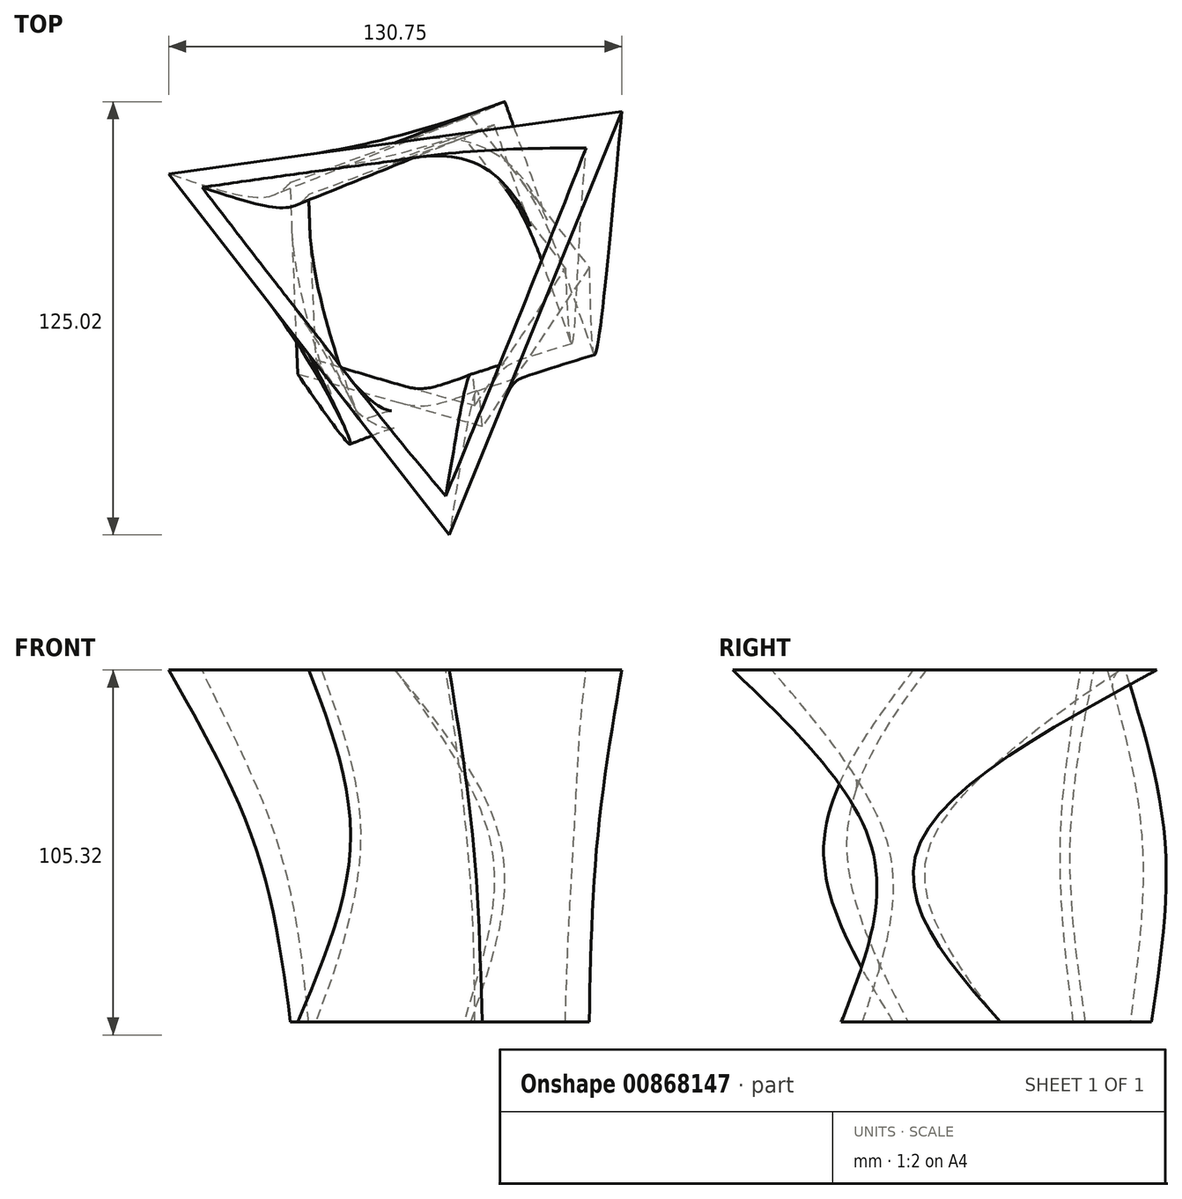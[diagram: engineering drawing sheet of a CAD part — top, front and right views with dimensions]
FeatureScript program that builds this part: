
annotation { "Feature Type Name" : "Feature", "Feature Type Description" : "" }
export const myFeature = defineFeature(function(context is Context, id is Id, definition is map)
    precondition{}
    {
        {
            var Q0;
            Q0=qCreatedBy(makeId("Top.planeOp"),FACE);
            var sketch = newSketch(context, id + "F0", { "sketchPlane" : qUnion([Q0])});
            skCircle(sketch, "E0.cCircle", {"center": v(0, 0) * mm, "radius": 38.1 * mm, "construction": true});
            skLineSegment(sketch, "E0.0", {"start": v(-39.1, 26.24) * mm, "end": v(12.87, 45.3) * mm});
            skLineSegment(sketch, "E0.1", {"start": v(12.87, 45.3) * mm, "end": v(47.06, 1.76) * mm});
            skLineSegment(sketch, "E0.2", {"start": v(47.06, 1.76) * mm, "end": v(16.21, -44.22) * mm});
            skLineSegment(sketch, "E0.3", {"start": v(16.21, -44.22) * mm, "end": v(-37.04, -29.08) * mm});
            skLineSegment(sketch, "E0.4", {"start": v(-37.04, -29.08) * mm, "end": v(-39.1, 26.24) * mm});
            skPoint(sketch, "E0.0.midPoint", {"position": v(-13.12, 35.77) * mm});
            skSolve(sketch);
        }
        {
            var Q0;
            Q0=qCreatedBy(makeId("Top.planeOp"),FACE);
            cPlane(context, id + "F1", {"entities" : qUnion([Q0]), "cplaneType" : CPlaneType.OFFSET, "offset" : 50.8 * mm, "width" : 152.4 * mm, "height" : 152.4 * mm});
        }
        {
            var Q0;
            Q0=qCreatedBy(id+"F1.planeOp",FACE);
            var sketch = newSketch(context, id + "F2", { "sketchPlane" : qUnion([Q0])});
            skCircle(sketch, "E1.cCircle", {"center": v(0, 0) * mm, "radius": 38.1 * mm, "construction": true});
            skLineSegment(sketch, "E1.0", {"start": v(-49.26, 21.84) * mm, "end": v(21.84, 49.26) * mm});
            skLineSegment(sketch, "E1.1", {"start": v(21.84, 49.26) * mm, "end": v(49.26, -21.84) * mm});
            skLineSegment(sketch, "E1.2", {"start": v(49.26, -21.84) * mm, "end": v(-21.84, -49.26) * mm});
            skLineSegment(sketch, "E1.3", {"start": v(-21.84, -49.26) * mm, "end": v(-49.26, 21.84) * mm});
            skPoint(sketch, "E1.0.midPoint", {"position": v(-13.71, 35.55) * mm});
            skLineSegment(sketch, "E2", {"start": v(-21.84, -49.26) * mm, "end": v(21.84, 49.26) * mm, "construction": true});
            skSolve(sketch);
        }
        {
            var Q0;
            Q0=qCreatedBy(id+"F1.planeOp",FACE);
            cPlane(context, id + "F3", {"entities" : qUnion([Q0]), "cplaneType" : CPlaneType.OFFSET, "offset" : 50.8 * mm, "width" : 152.4 * mm, "height" : 152.4 * mm});
        }
        {
            var Q0;
            Q0=qCreatedBy(id+"F3.planeOp",FACE);
            var sketch = newSketch(context, id + "F4", { "sketchPlane" : qUnion([Q0])});
            skCircle(sketch, "E3.cCircle", {"center": v(-3.69, 0) * mm, "radius": 38.1 * mm, "construction": true});
            skLineSegment(sketch, "E3.0", {"start": v(-74.27, 28.73) * mm, "end": v(56.48, 46.76) * mm});
            skLineSegment(sketch, "E3.1", {"start": v(56.48, 46.76) * mm, "end": v(6.72, -75.49) * mm});
            skLineSegment(sketch, "E3.2", {"start": v(6.72, -75.49) * mm, "end": v(-74.27, 28.73) * mm});
            skPoint(sketch, "E3.0.midPoint", {"position": v(-8.9, 37.74) * mm});
            skSolve(sketch);
        }
        {
            var Q0;
            Q0=makeQuery(id+"F0.imprint","IMPRINT",FACE,{"disambiguationData":[TD([[makeQuery(id+"F0.imprint","IMPRINT",EDGE,{"derivedFrom":sQuery(id+"F0.wireOp",EDGE,"E0.0")}),-1.0]])]});
            var Q1;
            Q1=makeQuery(id+"F2.imprint","IMPRINT",FACE,{"disambiguationData":[TD([[makeQuery(id+"F2.imprint","IMPRINT",EDGE,{"derivedFrom":sQuery(id+"F2.wireOp",EDGE,"E1.0")}),-1.0]])]});
            var Q2;
            Q2=makeQuery(id+"F4.imprint","IMPRINT",FACE,{"disambiguationData":[TD([[makeQuery(id+"F4.imprint","IMPRINT",EDGE,{"derivedFrom":sQuery(id+"F4.wireOp",EDGE,"E3.0")}),-1.0]])]});
            loft(context, id + "F5", {"sheetProfilesArray" : [{ "sheetProfileEntities" : qUnion([Q0]) }, { "sheetProfileEntities" : qUnion([Q1]) }, { "sheetProfileEntities" : qUnion([Q2]) }]});
        }
        {
            var Q0;
            Q0=makeQuery(id+"F5.opLoft","CAP_FACE",FACE,{"disambiguationData":[OSD([makeQuery(id+"F4.imprint","IMPRINT",FACE,{"disambiguationData":[TD([[makeQuery(id+"F4.imprint","IMPRINT",EDGE,{"derivedFrom":sQuery(id+"F4.wireOp",EDGE,"E3.0")}),-1.0]])]})])],"isStart":true});
            var Q1;
            Q1=makeQuery(id+"F5.opLoft","CAP_FACE",FACE,{"disambiguationData":[OSD([makeQuery(id+"F0.imprint","IMPRINT",FACE,{"disambiguationData":[TD([[makeQuery(id+"F0.imprint","IMPRINT",EDGE,{"derivedFrom":sQuery(id+"F0.wireOp",EDGE,"E0.0")}),-1.0]])]})])],"isStart":true});
            shell(context, id + "F6", {"entities" : qUnion([Q0, Q1]), "thickness" : 5.08 * mm});
        }
    });
